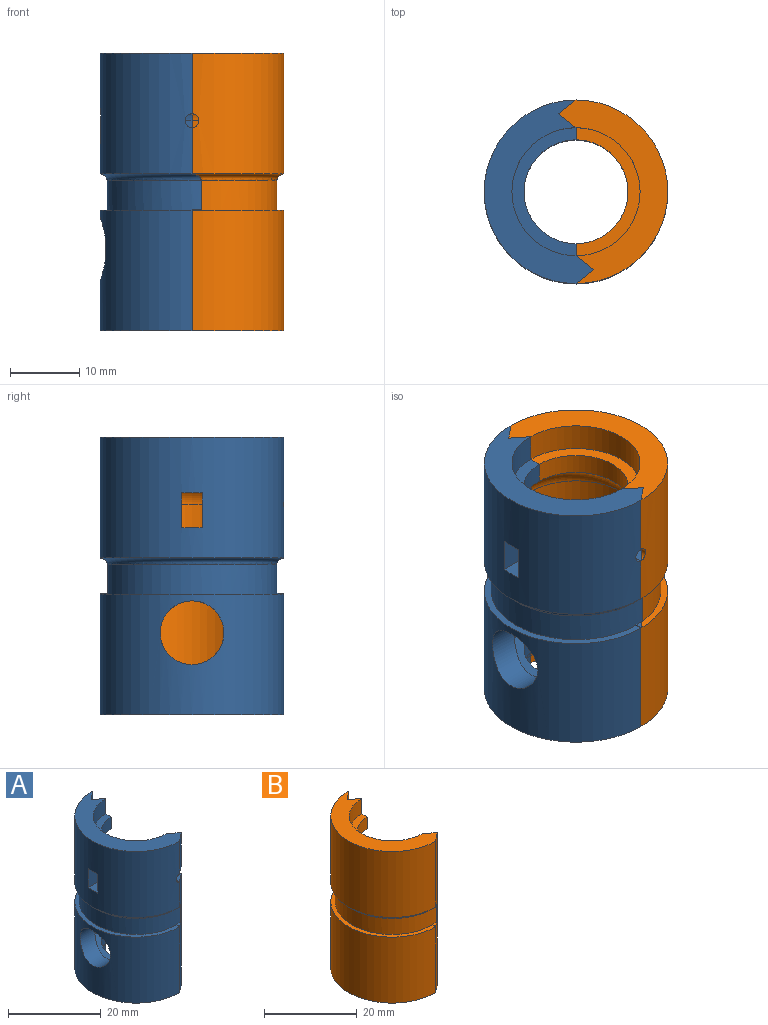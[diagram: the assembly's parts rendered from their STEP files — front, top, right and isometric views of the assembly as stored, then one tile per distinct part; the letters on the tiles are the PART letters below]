
ASSEMBLY  parts=2 mates=1
PART A: 38 faces, bbox 17.7x30.3x40 mm
  f0: cylinder r=13.25mm len=26.5mm, axis (0,0,-1), area 707.7mm2, adj f3,f10,f22,f24,f29,f30,f31,f32
  f1: cylinder r=9.25mm len=23.27mm, axis (0,0,-1), area 597mm2, adj f2,f4,f18,f25,f28,f30,f31,f32
  f2: plane 29.3x2.5mm, normal (0.62,0.78,0), area 93.8mm2, adj f1,f3,f9,f16,f17,f36
  f3: plane 29.3x2.5mm, normal (0.62,-0.78,0), area 85.5mm2, adj f0,f2,f5,f14,f15,f16,f23,f26
  f4: torus R=6.25mm, axis (0,0,1), area 86.5mm2, adj f1,f7,f8,f13,f29,f30,f31,f35
  f5: plane 0.44x0.1mm, normal (-1,0,0), area 0mm2, adj f3,f27,f34
  f6: plane 5.73x1.75mm, normal (1,0,0), area 6.6mm2, adj f18,f19,f25,f33
  f7: plane 5.73x1.75mm, normal (1,0,0), area 6.6mm2, adj f4,f12,f13,f25
  f8: plane 4.7x1.75mm, normal (1,0,0), area 6.5mm2, adj f4,f12,f13,f21,f35
  f9: plane 5.73x1.75mm, normal (1,0,0), area 6.6mm2, adj f2,f18,f19,f33
  f10: plane 26.5x15.75mm, normal (0,0,1), area 141.4mm2, adj f0,f11,f21,f22,f24,f25
  f11: cylinder r=9.25mm len=18.5mm, axis (0,0,1), area 116.2mm2, adj f10,f12,f21,f25
  f12: plane 18.5x9.25mm, normal (0,0,1), area 46mm2, adj f7,f8,f11,f13
  f13: cylinder r=7.5mm len=15mm, axis (0,0,-1), area 70.7mm2, adj f4,f7,f8,f12
  f14: cylinder r=12.25mm len=24.43mm, axis (0,0,-1), area 161.5mm2, adj f3,f20,f23,f24,f26,f34
  f15: cylinder r=13.25mm len=26.5mm, axis (0,0,1), area 656.8mm2, adj f3,f16,f20,f24,f28
  f16: plane 26.5x15.75mm, normal (0,0,-1), area 141.4mm2, adj f2,f3,f15,f17,f24,f25
  f17: cylinder r=9.25mm len=18.5mm, axis (0,0,-1), area 37mm2, adj f2,f16,f25,f33
  f18: plane 18.5x9.25mm, normal (0,0,1), area 46mm2, adj f1,f6,f9,f19
  f19: cylinder r=7.5mm len=15mm, axis (0,0,1), area 70.7mm2, adj f6,f9,f18,f33
  f20: plane 26.5x13.25mm, normal (0,0,1), area 39.4mm2, adj f14,f15,f23,f24
  f21: plane 8.7x2.5mm, normal (0.62,0.78,0), area 27.9mm2, adj f8,f10,f11,f22,f37
  f22: plane 8.7x2.5mm, normal (0.62,-0.78,0), area 27.9mm2, adj f0,f10,f21,f37
  f23: plane 1x0.1mm, normal (-1,0,0), area 0.1mm2, adj f3,f14,f20,f26
  f24: plane 40x2.5mm, normal (0.62,-0.78,0), area 119.5mm2, adj f0,f10,f14,f15,f16,f20,f25,f34
  f25: plane 40x2.5mm, normal (0.62,0.78,0), area 128.1mm2, adj f1,f6,f7,f10,f11,f16,f17,f24
  f26: plane 1.34x1.07mm, normal (0,0,1), area 0.7mm2, adj f3,f14,f23
  f27: plane 0.56x0.45mm, normal (0,0,-1), area 0.1mm2, adj f3,f5,f34
  f28: cylinder r=4.6mm len=9.2mm, axis (1,0,0), area 121.2mm2, adj f1,f15
  f29: plane 4.68x3mm, normal (0,0,-1), area 13.7mm2, adj f0,f4,f30,f31
  f30: plane 5.05x4.64mm, normal (0,-1,0), area 20.5mm2, adj f0,f1,f4,f29,f32
  f31: plane 5.05x4.64mm, normal (0,1,0), area 20.5mm2, adj f0,f1,f4,f29,f32
  f32: plane 4.12x3mm, normal (0,0,1), area 12mm2, adj f0,f1,f30,f31
  f33: torus R=6.25mm, axis (0,0,1), area 92.9mm2, adj f6,f9,f17,f19
  f34: torus R=13.25mm, axis (0,0,-1), area 62.1mm2, adj f0,f3,f5,f14,f24,f27
  f35: cylinder r=1mm len=4.18mm, axis (0,1,0), area 12.8mm2, adj f0,f1,f4,f8,f36,f37
  f36: plane 4x2.5mm, normal (0,0,1), area 5mm2, adj f2,f3,f35
  f37: plane 4x2.5mm, normal (0,0,-1), area 5mm2, adj f21,f22,f35
PART B: 30 faces, bbox 17.6x30.2x40 mm
  f0: plane 0.44x0.1mm, normal (-1,0,0), area 0mm2, adj f19,f24,f27
  f1: plane 5.73x1.75mm, normal (1,0,0), area 6.6mm2, adj f15,f16,f22,f26
  f2: plane 4.7x1.75mm, normal (1,0,0), area 6.5mm2, adj f8,f10,f22,f25,f28
  f3: plane 5.73x1.75mm, normal (1,0,0), area 6.6mm2, adj f8,f10,f18,f25
  f4: plane 5.73x1.75mm, normal (1,0,0), area 6.6mm2, adj f15,f16,f18,f26
  f5: cylinder r=13.25mm len=26.5mm, axis (0,0,-1), area 722.7mm2, adj f6,f19,f21,f27,f29
  f6: plane 26.5x15.75mm, normal (0,0,1), area 141.4mm2, adj f5,f7,f18,f19,f21,f22
  f7: cylinder r=9.25mm len=18.5mm, axis (0,0,1), area 116.2mm2, adj f6,f8,f18,f22
  f8: plane 18.5x9.25mm, normal (0,0,1), area 46mm2, adj f2,f3,f7,f10
  f9: cylinder r=9.25mm len=23.27mm, axis (0,0,-1), area 675.5mm2, adj f15,f18,f22,f25,f28
  f10: cylinder r=7.5mm len=15mm, axis (0,0,-1), area 70.7mm2, adj f2,f3,f8,f25
  f11: cylinder r=12.25mm len=24.43mm, axis (0,0,-1), area 161.5mm2, adj f17,f19,f20,f21,f23,f27
  f12: cylinder r=13.25mm len=26.5mm, axis (0,0,1), area 724.3mm2, adj f13,f17,f19,f21
  f13: plane 26.5x15.75mm, normal (0,0,-1), area 141.4mm2, adj f12,f14,f18,f19,f21,f22
  f14: cylinder r=9.25mm len=18.5mm, axis (0,0,-1), area 37mm2, adj f13,f18,f22,f26
  f15: plane 18.5x9.25mm, normal (0,0,1), area 46mm2, adj f1,f4,f9,f16
  f16: cylinder r=7.5mm len=15mm, axis (0,0,1), area 70.7mm2, adj f1,f4,f15,f26
  f17: plane 26.5x13.25mm, normal (0,0,1), area 39.4mm2, adj f11,f12,f20,f21
  f18: plane 40x2.5mm, normal (0.62,0.78,0), area 128.1mm2, adj f3,f4,f6,f7,f9,f13,f14,f19
  f19: plane 40x2.5mm, normal (0.62,-0.78,0), area 119.7mm2, adj f0,f5,f6,f11,f12,f13,f18,f20
  f20: plane 1x0.1mm, normal (-1,0,0), area 0.1mm2, adj f11,f17,f19,f23
  f21: plane 40x2.5mm, normal (0.62,-0.78,0), area 117.5mm2, adj f5,f6,f11,f12,f13,f17,f22,f27
  f22: plane 40x2.5mm, normal (0.62,0.78,0), area 126.1mm2, adj f1,f2,f6,f7,f9,f13,f14,f21
  f23: plane 1.34x1.07mm, normal (0,0,1), area 0.7mm2, adj f11,f19,f20
  f24: plane 0.56x0.45mm, normal (0,0,-1), area 0.1mm2, adj f0,f19,f27
  f25: torus R=6.25mm, axis (0,0,1), area 92.1mm2, adj f2,f3,f9,f10,f28
  f26: torus R=6.25mm, axis (0,0,1), area 92.9mm2, adj f1,f4,f14,f16
  f27: torus R=13.25mm, axis (0,0,-1), area 62.1mm2, adj f0,f5,f11,f19,f21,f24
  f28: cylinder r=1mm len=2mm, axis (0,-1,0), area 1.8mm2, adj f2,f9,f22,f25
  f29: cylinder r=1mm len=2mm, axis (0,-1,0), area 1.6mm2, adj f5,f21
PLACE A t=(-85.56,-25.1,5.2)mm
PLACE B rot(axis=(0,0,1),180deg) t=(-85.56,-25.1,5.2)mm
MATE fastened B.f3 <-> A.f7  axis (-1,0,0) through (-85.56,-16.64,19.26)mm
